# Revit family: MP 450 Combi (a)
name_source: partatom
category: Equipement spécialisé
revit_build: Autodesk Revit LT 2015 (Build: 20140606_1530(x64)
units: mm (PartAtom-declared; Revit-internal decimal feet)

## types (3) — shared parameters
Apparent Power = 0 VA
Depth = 125 mm  [stored 0.410105 ft]
Depth Electrique connexion = 63 mm
Description = MIXERS PLONGEANTS GAMME COMBI
Fabricant = ROBOT COUPE
Height Electrique connexion cloche = 880 mm
Height Electrique connexion fouet = 815 mm
Height cloche = 890 mm  [stored 2.91995 ft]
Height fouet = 825 mm
Modèle = MP 450 Combi
Phase = 1
Speeds (Rpm) = 1500 to 9000 (Mixer)  -  250 to 1500 (Whisk)
URL = www.robot-coupe.com
Watts = 500 W
Weight = 8.2 kg
Width cloche = 173 mm
Width fouet = 176 mm
water = Connector
zero-valued in all types: Cold water supply, Cold water supply height, Used water, Waste water height

## per-type parameters (varying)
| type | Amps | Cycle | Volts |
| MP 450 Combi   230/50/1 | 2.3 A | 50 Hz | 230 V |
| MP 450 Combi   120/60/1 | 4.5 A | 60 Hz | 120 V |
| MP 450 Combi   240/50/1 | 2.1 A | 50 Hz | 240 V |

note: [stored X ft] marks values corroborated as IEEE doubles in the binary element streams (Revit-internal decimal feet)

## geometry (parser evidence)
native form markers: Blend x85, Sweep x4
no freeform markers — native parametric forms only
